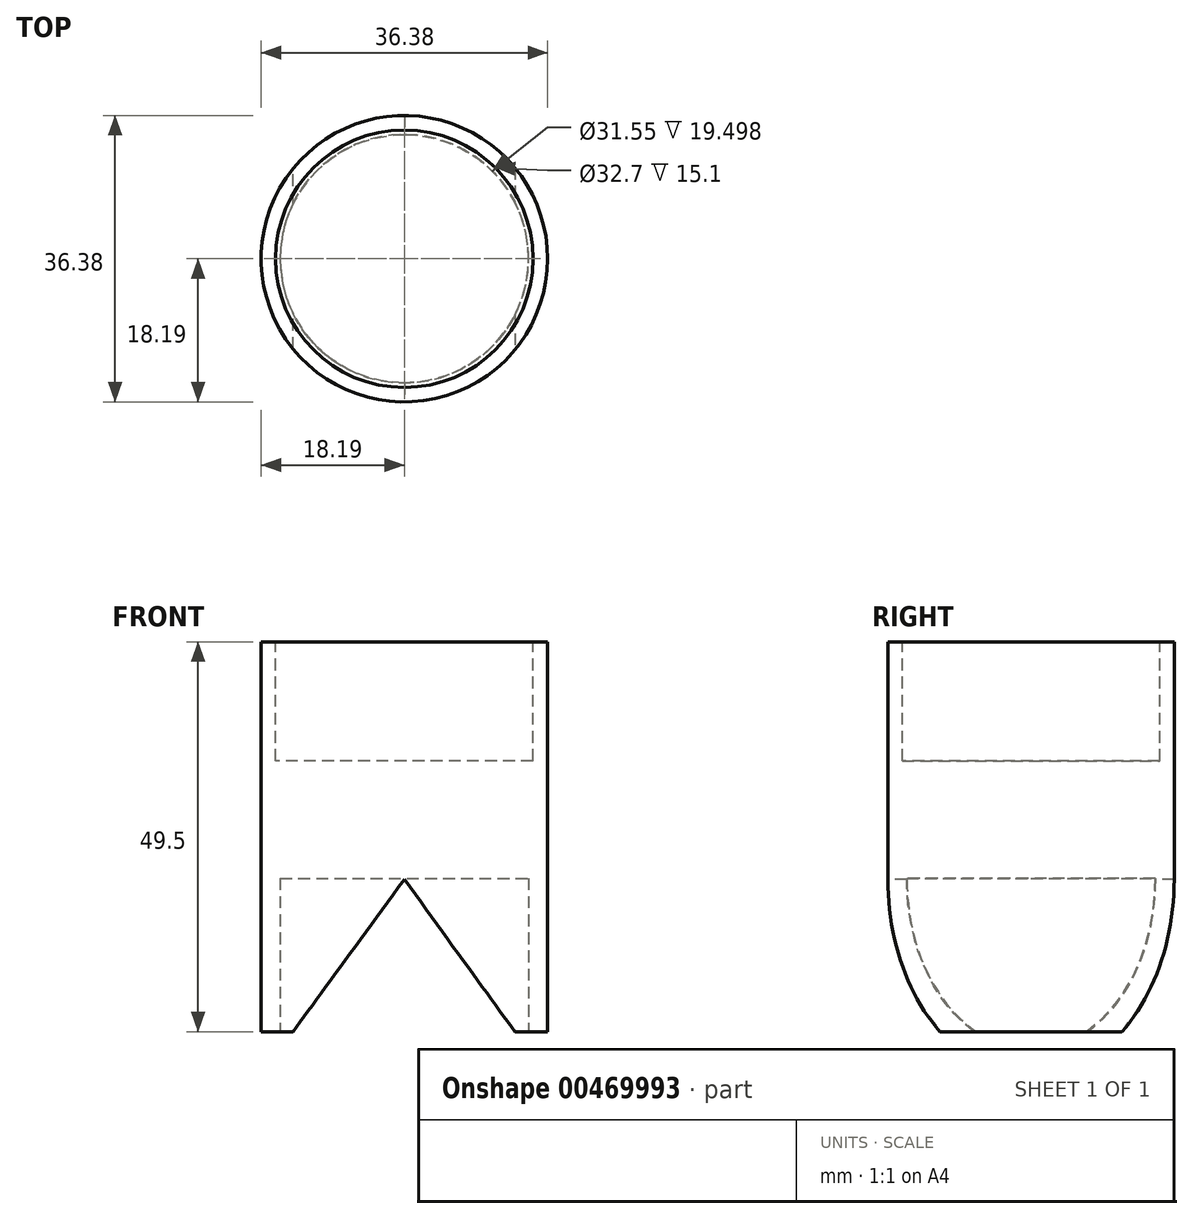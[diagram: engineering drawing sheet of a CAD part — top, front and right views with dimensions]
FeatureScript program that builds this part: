
annotation { "Feature Type Name" : "Feature", "Feature Type Description" : "" }
export const myFeature = defineFeature(function(context is Context, id is Id, definition is map)
    precondition{}
    {
        {
            var Q0;
            Q0=qCreatedBy(makeId("Top.planeOp"),FACE);
            var sketch = newSketch(context, id + "F0", { "sketchPlane" : qUnion([Q0])});
            skCircle(sketch, "E0", {"center": v(0, 0) * mm, "radius": 18.2 * mm});
            skSolve(sketch);
        }
        {
            var Q0;
            Q0 = qSketchRegion(id + "F0", true);
            extrude(context, id + "F1", {"entities" : qUnion([Q0]), "depth" : 30 * mm, "offsetDistance" : 25 * mm});
        }
        {
            var Q0;
            Q0=makeQuery(id+"F1.opExtrude","CAP_FACE",FACE,{"disambiguationData":[OSD([sQuery(id+"F0.wireOp",EDGE,"E0")])],"isStart":true});
            var sketch = newSketch(context, id + "F2", { "sketchPlane" : qUnion([Q0])});
            skCircle(sketch, "E1", {"center": v(0, 0) * mm, "radius": 15.77 * mm});
            skSolve(sketch);
        }
        {
            var Q0;
            Q0=makeQuery(id+"F2.imprint","IMPRINT",FACE,{"disambiguationData":[TD([[makeQuery(id+"F2.imprint","IMPRINT",EDGE,{"derivedFrom":sQuery(id+"F2.wireOp",EDGE,"E1")}),1.0]])]});
            extrude(context, id + "F3", {"entities" : qUnion([Q0]), "operationType" : NewBodyOperationType.REMOVE, "oppositeDirection" : true, "depth" : 25 * mm, "offsetDistance" : 25 * mm});
        }
        {
            var Q0;
            Q0=qCreatedBy(makeId("Front.planeOp"),FACE);
            var sketch = newSketch(context, id + "F4", { "sketchPlane" : qUnion([Q0])});
            skLineSegment(sketch, "E2", {"start": v(-18.19, 0) * mm, "end": v(0, 24.83) * mm});
            skLineSegment(sketch, "E3", {"start": v(0, 24.83) * mm, "end": v(18.04, 0) * mm});
            skLineSegment(sketch, "E4", {"start": v(18.04, 0) * mm, "end": v(-18.19, 0) * mm});
            skSolve(sketch);
        }
        {
            var Q0;
            Q0 = qSketchRegion(id + "F4", true);
            extrude(context, id + "F5", {"entities" : qUnion([Q0]), "operationType" : NewBodyOperationType.REMOVE, "oppositeDirection" : true, "depth" : 25 * mm, "offsetDistance" : 25 * mm, "hasSecondDirection" : true, "secondDirectionOppositeDirection" : false, "secondDirectionDepth" : 25 * mm});
        }
        {
            var Q0;
            Q0=qCreatedBy(makeId("Front.planeOp"),FACE);
            var sketch = newSketch(context, id + "F6", { "sketchPlane" : qUnion([Q0])});
            skLineSegment(sketch, "E5.bottom", {"start": v(-25.22, 5.5) * mm, "end": v(25.22, 5.5) * mm});
            skLineSegment(sketch, "E5.top", {"start": v(-25.22, -25.12) * mm, "end": v(25.22, -25.12) * mm});
            skLineSegment(sketch, "E5.left", {"start": v(-25.22, 5.5) * mm, "end": v(-25.22, -25.12) * mm});
            skLineSegment(sketch, "E5.right", {"start": v(25.22, 5.5) * mm, "end": v(25.22, -25.12) * mm});
            skPoint(sketch, "E5.middle", {"position": v(0, -9.8) * mm});
            skSolve(sketch);
        }
        {
            var Q0;
            Q0=makeQuery(id+"F6.imprint","IMPRINT",FACE,{"disambiguationData":[TD([[makeQuery(id+"F6.imprint","IMPRINT",EDGE,{"derivedFrom":sQuery(id+"F6.wireOp",EDGE,"E5.bottom")}),-1.0]])]});
            extrude(context, id + "F7", {"entities" : qUnion([Q0]), "operationType" : NewBodyOperationType.REMOVE, "oppositeDirection" : true, "depth" : 25 * mm, "offsetDistance" : 25 * mm, "hasSecondDirection" : true, "secondDirectionOppositeDirection" : false, "secondDirectionDepth" : 25 * mm});
        }
        {
            var Q0;
            Q0=makeQuery(id+"F1.opExtrude","CAP_FACE",FACE,{"disambiguationData":[OSD([sQuery(id+"F0.wireOp",EDGE,"E0")])],"isStart":false});
            extrude(context, id + "F8", {"entities" : qUnion([Q0]), "operationType" : NewBodyOperationType.ADD, "depth" : 25 * mm, "offsetDistance" : 25 * mm});
        }
        {
            var Q0;
            Q0=makeQuery(id+"F8.opExtrude","CAP_FACE",FACE,{"disambiguationData":[OSD([sQuery(id+"F0.wireOp",EDGE,"E0")])],"isStart":false});
            var sketch = newSketch(context, id + "F9", { "sketchPlane" : qUnion([Q0])});
            skCircle(sketch, "E6", {"center": v(0, 0) * mm, "radius": 16.35 * mm});
            skSolve(sketch);
        }
        {
            var Q0;
            Q0=makeQuery(id+"F9.imprint","IMPRINT",FACE,{"disambiguationData":[TD([[makeQuery(id+"F9.imprint","IMPRINT",EDGE,{"derivedFrom":sQuery(id+"F9.wireOp",EDGE,"E6")}),1.0]])]});
            extrude(context, id + "F10", {"entities" : qUnion([Q0]), "operationType" : NewBodyOperationType.REMOVE, "oppositeDirection" : true, "depth" : 15.1 * mm, "offsetDistance" : 25 * mm});
        }
    });
